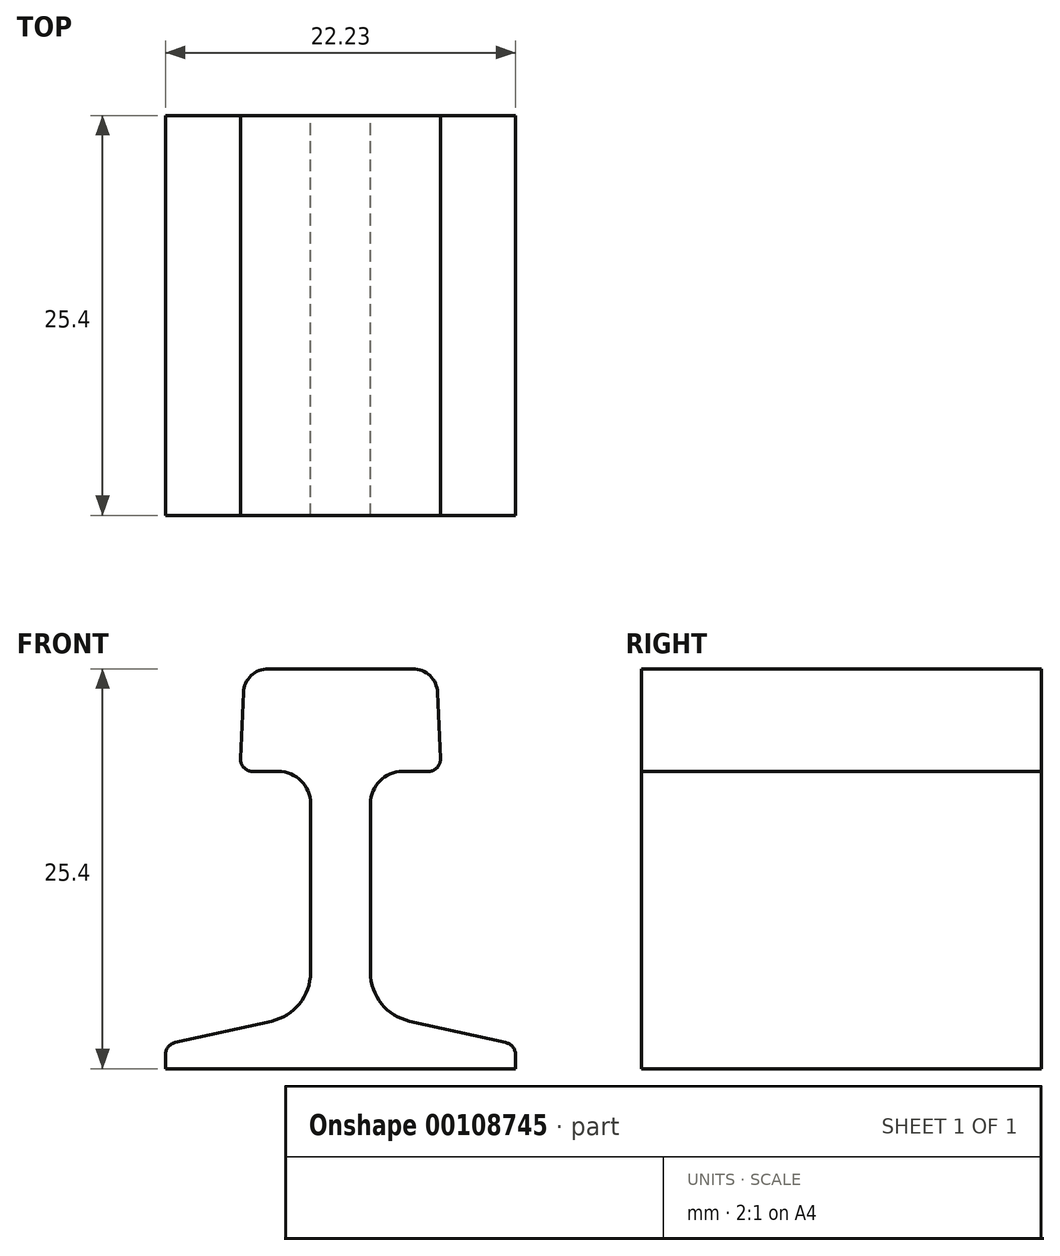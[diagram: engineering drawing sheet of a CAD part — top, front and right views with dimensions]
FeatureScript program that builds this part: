
annotation { "Feature Type Name" : "Feature", "Feature Type Description" : "" }
export const myFeature = defineFeature(function(context is Context, id is Id, definition is map)
    precondition{}
    {
        {
            var Q0;
            Q0=qCreatedBy(makeId("Front.planeOp"),FACE);
            var sketch = newSketch(context, id + "F0", { "sketchPlane" : qUnion([Q0])});
            skLineSegment(sketch, "E0", {"start": v(0, 0) * mm, "end": v(22.23, 0) * mm});
            skLineSegment(sketch, "E1", {"start": v(22.23, 0) * mm, "end": v(22.23, 0.89) * mm});
            skLineSegment(sketch, "E2", {"start": v(21.6, 1.66) * mm, "end": v(15.5, 3.01) * mm});
            skLineSegment(sketch, "E3", {"start": v(13.02, 6.11) * mm, "end": v(13.02, 16.84) * mm});
            skLineSegment(sketch, "E4", {"start": v(15.05, 18.87) * mm, "end": v(16.67, 18.87) * mm});
            skLineSegment(sketch, "E5", {"start": v(17.46, 19.7) * mm, "end": v(17.28, 23.88) * mm});
            skLineSegment(sketch, "E6", {"start": v(15.7, 25.4) * mm, "end": v(6.53, 25.4) * mm});
            skLineSegment(sketch, "E7", {"start": v(4.94, 23.88) * mm, "end": v(4.76, 19.7) * mm});
            skLineSegment(sketch, "E8", {"start": v(5.55, 18.87) * mm, "end": v(7.18, 18.87) * mm});
            skLineSegment(sketch, "E9", {"start": v(9.2, 16.84) * mm, "end": v(9.2, 6.11) * mm});
            skLineSegment(sketch, "E10", {"start": v(6.72, 3.01) * mm, "end": v(0.62, 1.66) * mm});
            skLineSegment(sketch, "E11", {"start": v(0, 0.89) * mm, "end": v(0, 0) * mm});
            skPoint(sketch, "E12.visualSharp", {"position": v(9.2, 18.87) * mm});
            skArc(sketch, "E12.filletArc", {"start": v(9.2, 16.84) * mm, "mid": v(8.61, 18.28) * mm, "end": v(7.18, 18.87) * mm});
            skPoint(sketch, "E13.visualSharp", {"position": v(13.02, 18.87) * mm});
            skArc(sketch, "E13.filletArc", {"start": v(15.05, 18.87) * mm, "mid": v(13.61, 18.28) * mm, "end": v(13.02, 16.84) * mm});
            skPoint(sketch, "E14.visualSharp", {"position": v(5, 25.4) * mm});
            skArc(sketch, "E14.filletArc", {"start": v(6.53, 25.4) * mm, "mid": v(5.43, 24.96) * mm, "end": v(4.94, 23.88) * mm});
            skPoint(sketch, "E15.visualSharp", {"position": v(17.22, 25.4) * mm});
            skArc(sketch, "E15.filletArc", {"start": v(17.28, 23.88) * mm, "mid": v(16.8, 24.96) * mm, "end": v(15.7, 25.4) * mm});
            skPoint(sketch, "E16.visualSharp", {"position": v(4.72, 18.87) * mm});
            skArc(sketch, "E16.filletArc", {"start": v(4.76, 19.7) * mm, "mid": v(4.98, 19.12) * mm, "end": v(5.55, 18.87) * mm});
            skPoint(sketch, "E17.visualSharp", {"position": v(17.5, 18.87) * mm});
            skArc(sketch, "E17.filletArc", {"start": v(16.67, 18.87) * mm, "mid": v(17.24, 19.12) * mm, "end": v(17.46, 19.7) * mm});
            skPoint(sketch, "E18.visualSharp", {"position": v(0, 1.52) * mm});
            skArc(sketch, "E18.filletArc", {"start": v(0.62, 1.66) * mm, "mid": v(0.17, 1.38) * mm, "end": v(0, 0.89) * mm});
            skPoint(sketch, "E19.visualSharp", {"position": v(22.23, 1.52) * mm});
            skArc(sketch, "E19.filletArc", {"start": v(22.23, 0.89) * mm, "mid": v(22.05, 1.38) * mm, "end": v(21.6, 1.66) * mm});
            skPoint(sketch, "E20.visualSharp", {"position": v(9.2, 3.57) * mm});
            skArc(sketch, "E20.filletArc", {"start": v(6.72, 3.01) * mm, "mid": v(8.5, 4.13) * mm, "end": v(9.2, 6.11) * mm});
            skPoint(sketch, "E21.visualSharp", {"position": v(13.02, 3.57) * mm});
            skArc(sketch, "E21.filletArc", {"start": v(13.02, 6.11) * mm, "mid": v(13.72, 4.13) * mm, "end": v(15.5, 3.01) * mm});
            skSolve(sketch);
        }
        {
            var Q0;
            Q0=makeQuery(id+"F0.imprint","IMPRINT",FACE,{"disambiguationData":[TD([[makeQuery(id+"F0.imprint","IMPRINT",EDGE,{"derivedFrom":sQuery(id+"F0.wireOp",EDGE,"E0")}),1.0]])]});
            extrude(context, id + "F1", {"entities" : qUnion([Q0]), "flatOperationType" : FlatOperationType.REMOVE, "offsetDistance" : 25.4 * mm, "depth" : 25.4 * mm, "domain" : OperationDomain.MODEL});
        }
    });
